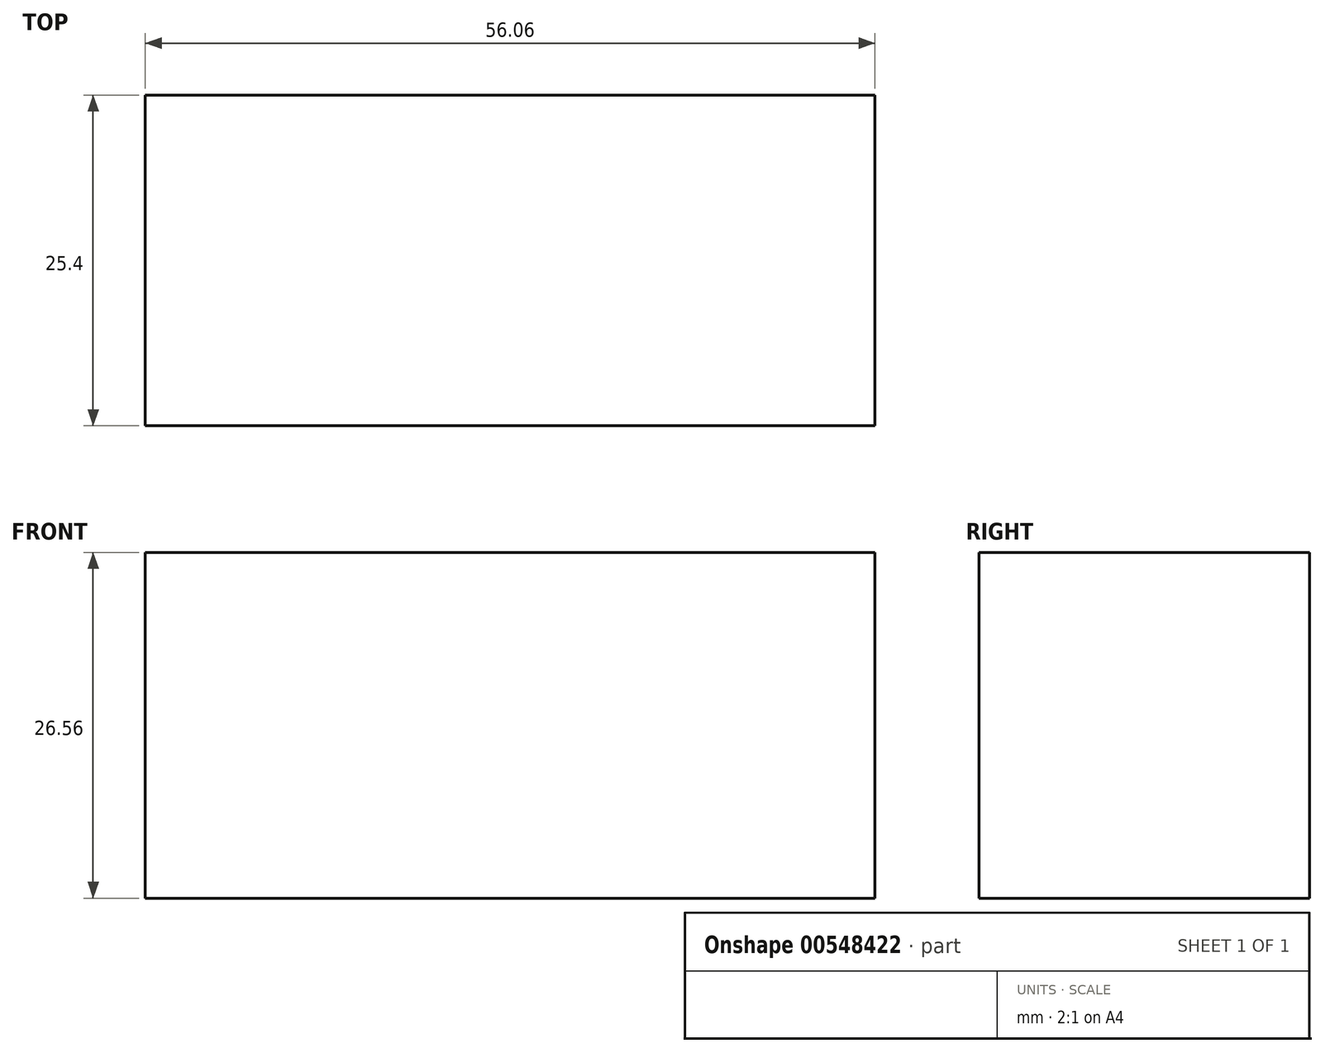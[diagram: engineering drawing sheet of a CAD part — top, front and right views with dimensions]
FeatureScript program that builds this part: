
annotation { "Feature Type Name" : "Feature", "Feature Type Description" : "" }
export const myFeature = defineFeature(function(context is Context, id is Id, definition is map)
    precondition{}
    {
        {
            var Q0;
            Q0=qCreatedBy(makeId("Front.planeOp"),FACE);
            var sketch = newSketch(context, id + "F0", { "sketchPlane" : qUnion([Q0])});
            skLineSegment(sketch, "E0.bottom", {"start": v(3.44, 0) * mm, "end": v(-52.62, 0) * mm});
            skLineSegment(sketch, "E0.top", {"start": v(3.44, 26.56) * mm, "end": v(-52.62, 26.56) * mm});
            skLineSegment(sketch, "E0.left", {"start": v(3.44, 0) * mm, "end": v(3.44, 26.56) * mm});
            skLineSegment(sketch, "E0.right", {"start": v(-52.62, 0) * mm, "end": v(-52.62, 26.56) * mm});
            skSolve(sketch);
        }
        {
            var Q0;
            Q0 = qSketchRegion(id + "F0", true);
            extrude(context, id + "F1", {"entities" : qUnion([Q0]), "depth" : 25.4 * mm, "offsetDistance" : 25.4 * mm});
        }
    });
